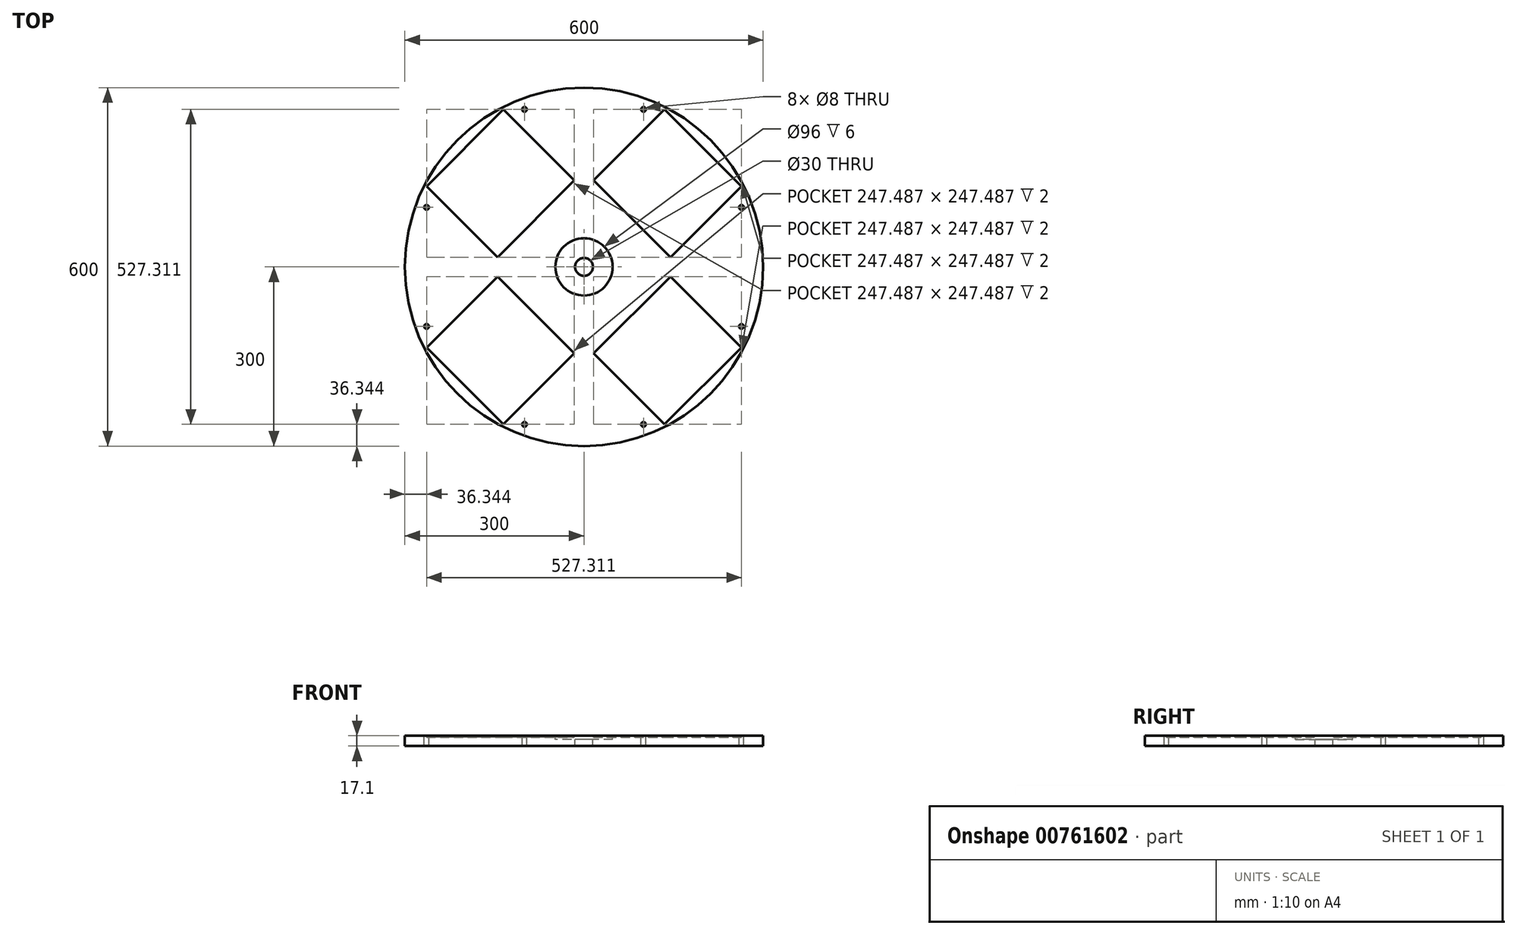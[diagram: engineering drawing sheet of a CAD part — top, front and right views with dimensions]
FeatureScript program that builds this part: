
annotation { "Feature Type Name" : "Feature", "Feature Type Description" : "" }
export const myFeature = defineFeature(function(context is Context, id is Id, definition is map)
    precondition{}
    {
        {
            var Q0;
            Q0=qCreatedBy(makeId("Top.planeOp"),FACE);
            var sketch = newSketch(context, id + "F0", { "sketchPlane" : qUnion([Q0])});
            skCircle(sketch, "E0", {"center": v(0, 0) * mm, "radius": 300 * mm});
            skSolve(sketch);
        }
        {
            var Q0;
            Q0 = qSketchRegion(id + "F0", true);
            var Q1;
            Q1=makeQuery(id+"F0.imprint","IMPRINT",FACE,{"disambiguationData":[TD([[makeQuery(id+"F0.imprint","IMPRINT",EDGE,{"derivedFrom":sQuery(id+"F0.wireOp",EDGE,"AllwrVL7-AkE9-LfNM-VB61-ajPjN6t2vvd7.bottom")}),-1.0]])]});
            var Q2;
            Q2=makeQuery(id+"F0.imprint","IMPRINT",FACE,{"disambiguationData":[TD([[makeQuery(id+"F0.imprint","IMPRINT",EDGE,{"derivedFrom":sQuery(id+"F0.wireOp",EDGE,"5d97284d-aa32-4368-b48b-b87623f71f09.3.0")}),1.0]])]});
            var Q3;
            Q3=makeQuery(id+"F0.imprint","IMPRINT",FACE,{"disambiguationData":[TD([[makeQuery(id+"F0.imprint","IMPRINT",EDGE,{"derivedFrom":sQuery(id+"F0.wireOp",EDGE,"5d97284d-aa32-4368-b48b-b87623f71f09.2.0")}),1.0]])]});
            var Q4;
            Q4=makeQuery(id+"F0.imprint","IMPRINT",FACE,{"disambiguationData":[TD([[makeQuery(id+"F0.imprint","IMPRINT",EDGE,{"derivedFrom":sQuery(id+"F0.wireOp",EDGE,"5d97284d-aa32-4368-b48b-b87623f71f09.1.0")}),1.0]])]});
            extrude(context, id + "F1", {"entities" : qUnion([Q0, Q1, Q2, Q3, Q4]), "depth" : 17.1 * mm, "offsetDistance" : 25 * mm});
        }
        {
            var Q0;
            Q0=makeQuery(id+"F1.opExtrude","CAP_FACE",FACE,{"disambiguationData":[OSD([sQuery(id+"F0.wireOp",EDGE,"E0"),sQuery(id+"F0.wireOp",EDGE,"m1Yok3GX-FKcm-f6FL-vg4J-QwZKevZHBzbs.bottom"),sQuery(id+"F0.wireOp",EDGE,"m1Yok3GX-FKcm-f6FL-vg4J-QwZKevZHBzbs.top"),sQuery(id+"F0.wireOp",EDGE,"m1Yok3GX-FKcm-f6FL-vg4J-QwZKevZHBzbs.left"),sQuery(id+"F0.wireOp",EDGE,"m1Yok3GX-FKcm-f6FL-vg4J-QwZKevZHBzbs.right"),sQuery(id+"F0.wireOp",EDGE,"c3f3dfe4-16c6-495d-901e-fd32c168dcf2.1.0"),sQuery(id+"F0.wireOp",EDGE,"c3f3dfe4-16c6-495d-901e-fd32c168dcf2.1.1"),sQuery(id+"F0.wireOp",EDGE,"c3f3dfe4-16c6-495d-901e-fd32c168dcf2.1.2"),sQuery(id+"F0.wireOp",EDGE,"c3f3dfe4-16c6-495d-901e-fd32c168dcf2.1.3"),sQuery(id+"F0.wireOp",EDGE,"c3f3dfe4-16c6-495d-901e-fd32c168dcf2.2.0"),sQuery(id+"F0.wireOp",EDGE,"c3f3dfe4-16c6-495d-901e-fd32c168dcf2.2.1"),sQuery(id+"F0.wireOp",EDGE,"c3f3dfe4-16c6-495d-901e-fd32c168dcf2.2.2"),sQuery(id+"F0.wireOp",EDGE,"c3f3dfe4-16c6-495d-901e-fd32c168dcf2.2.3"),sQuery(id+"F0.wireOp",EDGE,"c3f3dfe4-16c6-495d-901e-fd32c168dcf2.3.0"),sQuery(id+"F0.wireOp",EDGE,"c3f3dfe4-16c6-495d-901e-fd32c168dcf2.3.1"),sQuery(id+"F0.wireOp",EDGE,"c3f3dfe4-16c6-495d-901e-fd32c168dcf2.3.2"),sQuery(id+"F0.wireOp",EDGE,"c3f3dfe4-16c6-495d-901e-fd32c168dcf2.3.3"),sQuery(id+"F0.wireOp",EDGE,"GgWlmIyM-ttYd-3ydM-N6fe-A3lpZPIy1D6L"),sQuery(id+"F0.wireOp",EDGE,"be6c052b-b5ba-4b0f-ad13-1682f92d27ab0.MirrorC"),sQuery(id+"F0.wireOp",EDGE,"65b34546-e90f-493b-8633-af6543c614b7.1.0"),sQuery(id+"F0.wireOp",EDGE,"65b34546-e90f-493b-8633-af6543c614b7.1.1"),sQuery(id+"F0.wireOp",EDGE,"65b34546-e90f-493b-8633-af6543c614b7.2.0"),sQuery(id+"F0.wireOp",EDGE,"65b34546-e90f-493b-8633-af6543c614b7.2.1"),sQuery(id+"F0.wireOp",EDGE,"65b34546-e90f-493b-8633-af6543c614b7.3.0"),sQuery(id+"F0.wireOp",EDGE,"65b34546-e90f-493b-8633-af6543c614b7.3.1"),sQuery(id+"F0.wireOp",EDGE,"Zrx7hTxE-zzg4-Czgn-36LA-upzHOa7QcTNY"),sQuery(id+"F0.wireOp",EDGE,"a1d9c7c6-3c1d-4fec-942b-8c6368d16cfa0.MirrorC"),sQuery(id+"F0.wireOp",EDGE,"64f4d127-5a3c-484e-af48-e4f96c13fd4a.1.0"),sQuery(id+"F0.wireOp",EDGE,"64f4d127-5a3c-484e-af48-e4f96c13fd4a.1.1"),sQuery(id+"F0.wireOp",EDGE,"64f4d127-5a3c-484e-af48-e4f96c13fd4a.2.0"),sQuery(id+"F0.wireOp",EDGE,"64f4d127-5a3c-484e-af48-e4f96c13fd4a.2.1"),sQuery(id+"F0.wireOp",EDGE,"64f4d127-5a3c-484e-af48-e4f96c13fd4a.3.0"),sQuery(id+"F0.wireOp",EDGE,"64f4d127-5a3c-484e-af48-e4f96c13fd4a.3.1")])],"isStart":false});
            var sketch = newSketch(context, id + "F2", { "sketchPlane" : qUnion([Q0])});
            skLineSegment(sketch, "E1", {"start": v(0, 0) * mm, "end": v(-212.13, -212.13) * mm, "construction": true});
            skLineSegment(sketch, "E2", {"start": v(0, 0) * mm, "end": v(-300, 0) * mm, "construction": true});
            skLineSegment(sketch, "E3", {"start": v(-263.66, -134.96) * mm, "end": v(-134.96, -263.66) * mm});
            skLineSegment(sketch, "E4", {"start": v(-134.96, -263.66) * mm, "end": v(-16.17, -144.86) * mm});
            skLineSegment(sketch, "E5", {"start": v(-16.17, -144.86) * mm, "end": v(-144.86, -16.17) * mm});
            skLineSegment(sketch, "E6", {"start": v(-144.86, -16.17) * mm, "end": v(-263.66, -134.96) * mm});
            skPoint(sketch, "E7", {"position": v(-199.3, -199.3) * mm});
            skLineSegment(sketch, "E8", {"start": v(0, 0) * mm, "end": v(212.13, 212.13) * mm, "construction": true});
            skLineSegment(sketch, "E9", {"start": v(0, 0) * mm, "end": v(212.13, -212.13) * mm, "construction": true});
            skLineSegment(sketch, "E10", {"start": v(-263.66, -134.96) * mm, "end": v(-266.48, -137.8) * mm});
            skLineSegment(sketch, "E11.1.0", {"start": v(16.17, -144.86) * mm, "end": v(134.96, -263.66) * mm});
            skLineSegment(sketch, "E11.1.1", {"start": v(144.86, -16.17) * mm, "end": v(16.17, -144.86) * mm});
            skLineSegment(sketch, "E11.1.2", {"start": v(263.66, -134.96) * mm, "end": v(144.86, -16.17) * mm});
            skLineSegment(sketch, "E11.1.3", {"start": v(134.96, -263.66) * mm, "end": v(263.66, -134.96) * mm});
            skLineSegment(sketch, "E11.2.0", {"start": v(144.86, 16.17) * mm, "end": v(263.66, 134.96) * mm});
            skLineSegment(sketch, "E11.2.1", {"start": v(16.17, 144.86) * mm, "end": v(144.86, 16.17) * mm});
            skLineSegment(sketch, "E11.2.2", {"start": v(134.96, 263.66) * mm, "end": v(16.17, 144.86) * mm});
            skLineSegment(sketch, "E11.2.3", {"start": v(263.66, 134.96) * mm, "end": v(134.96, 263.66) * mm});
            skLineSegment(sketch, "E11.3.0", {"start": v(-16.17, 144.86) * mm, "end": v(-134.96, 263.66) * mm});
            skLineSegment(sketch, "E11.3.1", {"start": v(-144.86, 16.17) * mm, "end": v(-16.17, 144.86) * mm});
            skLineSegment(sketch, "E11.3.2", {"start": v(-263.66, 134.96) * mm, "end": v(-144.86, 16.17) * mm});
            skLineSegment(sketch, "E11.3.3", {"start": v(-134.96, 263.66) * mm, "end": v(-263.66, 134.96) * mm});
            skPoint(sketch, "E11.center", {"position": v(0, 0) * mm});
            skSolve(sketch);
        }
        {
            var Q0;
            Q0=qSketchRegion(id+"F2",true);
            extrude(context, id + "F3", {"entities" : qUnion([Q0]), "operationType" : NewBodyOperationType.REMOVE, "oppositeDirection" : true, "depth" : 2 * mm, "offsetDistance" : 25 * mm});
        }
        {
            var Q0;
            Q0=makeQuery(id+"F1.opExtrude","CAP_FACE",FACE,{"disambiguationData":[OSD([sQuery(id+"F0.wireOp",EDGE,"E0"),sQuery(id+"F0.wireOp",EDGE,"m1Yok3GX-FKcm-f6FL-vg4J-QwZKevZHBzbs.bottom"),sQuery(id+"F0.wireOp",EDGE,"m1Yok3GX-FKcm-f6FL-vg4J-QwZKevZHBzbs.top"),sQuery(id+"F0.wireOp",EDGE,"m1Yok3GX-FKcm-f6FL-vg4J-QwZKevZHBzbs.left"),sQuery(id+"F0.wireOp",EDGE,"m1Yok3GX-FKcm-f6FL-vg4J-QwZKevZHBzbs.right"),sQuery(id+"F0.wireOp",EDGE,"c3f3dfe4-16c6-495d-901e-fd32c168dcf2.1.0"),sQuery(id+"F0.wireOp",EDGE,"c3f3dfe4-16c6-495d-901e-fd32c168dcf2.1.1"),sQuery(id+"F0.wireOp",EDGE,"c3f3dfe4-16c6-495d-901e-fd32c168dcf2.1.2"),sQuery(id+"F0.wireOp",EDGE,"c3f3dfe4-16c6-495d-901e-fd32c168dcf2.1.3"),sQuery(id+"F0.wireOp",EDGE,"c3f3dfe4-16c6-495d-901e-fd32c168dcf2.2.0"),sQuery(id+"F0.wireOp",EDGE,"c3f3dfe4-16c6-495d-901e-fd32c168dcf2.2.1"),sQuery(id+"F0.wireOp",EDGE,"c3f3dfe4-16c6-495d-901e-fd32c168dcf2.2.2"),sQuery(id+"F0.wireOp",EDGE,"c3f3dfe4-16c6-495d-901e-fd32c168dcf2.2.3"),sQuery(id+"F0.wireOp",EDGE,"c3f3dfe4-16c6-495d-901e-fd32c168dcf2.3.0"),sQuery(id+"F0.wireOp",EDGE,"c3f3dfe4-16c6-495d-901e-fd32c168dcf2.3.1"),sQuery(id+"F0.wireOp",EDGE,"c3f3dfe4-16c6-495d-901e-fd32c168dcf2.3.2"),sQuery(id+"F0.wireOp",EDGE,"c3f3dfe4-16c6-495d-901e-fd32c168dcf2.3.3"),sQuery(id+"F0.wireOp",EDGE,"GgWlmIyM-ttYd-3ydM-N6fe-A3lpZPIy1D6L"),sQuery(id+"F0.wireOp",EDGE,"be6c052b-b5ba-4b0f-ad13-1682f92d27ab0.MirrorC"),sQuery(id+"F0.wireOp",EDGE,"65b34546-e90f-493b-8633-af6543c614b7.1.0"),sQuery(id+"F0.wireOp",EDGE,"65b34546-e90f-493b-8633-af6543c614b7.1.1"),sQuery(id+"F0.wireOp",EDGE,"65b34546-e90f-493b-8633-af6543c614b7.2.0"),sQuery(id+"F0.wireOp",EDGE,"65b34546-e90f-493b-8633-af6543c614b7.2.1"),sQuery(id+"F0.wireOp",EDGE,"65b34546-e90f-493b-8633-af6543c614b7.3.0"),sQuery(id+"F0.wireOp",EDGE,"65b34546-e90f-493b-8633-af6543c614b7.3.1"),sQuery(id+"F0.wireOp",EDGE,"Zrx7hTxE-zzg4-Czgn-36LA-upzHOa7QcTNY"),sQuery(id+"F0.wireOp",EDGE,"a1d9c7c6-3c1d-4fec-942b-8c6368d16cfa0.MirrorC"),sQuery(id+"F0.wireOp",EDGE,"64f4d127-5a3c-484e-af48-e4f96c13fd4a.1.0"),sQuery(id+"F0.wireOp",EDGE,"64f4d127-5a3c-484e-af48-e4f96c13fd4a.1.1"),sQuery(id+"F0.wireOp",EDGE,"64f4d127-5a3c-484e-af48-e4f96c13fd4a.2.0"),sQuery(id+"F0.wireOp",EDGE,"64f4d127-5a3c-484e-af48-e4f96c13fd4a.2.1"),sQuery(id+"F0.wireOp",EDGE,"64f4d127-5a3c-484e-af48-e4f96c13fd4a.3.0"),sQuery(id+"F0.wireOp",EDGE,"64f4d127-5a3c-484e-af48-e4f96c13fd4a.3.1"),sQuery(id+"F0.wireOp",EDGE,"AllwrVL7-AkE9-LfNM-VB61-ajPjN6t2vvd7.bottom"),sQuery(id+"F0.wireOp",EDGE,"AllwrVL7-AkE9-LfNM-VB61-ajPjN6t2vvd7.top"),sQuery(id+"F0.wireOp",EDGE,"AllwrVL7-AkE9-LfNM-VB61-ajPjN6t2vvd7.left"),sQuery(id+"F0.wireOp",EDGE,"AllwrVL7-AkE9-LfNM-VB61-ajPjN6t2vvd7.right"),sQuery(id+"F0.wireOp",EDGE,"vhIM6kYj-bil8-T5aC-Hw9W-HzG7wACOchpu.bottom"),sQuery(id+"F0.wireOp",EDGE,"vhIM6kYj-bil8-T5aC-Hw9W-HzG7wACOchpu.top"),sQuery(id+"F0.wireOp",EDGE,"vhIM6kYj-bil8-T5aC-Hw9W-HzG7wACOchpu.left"),sQuery(id+"F0.wireOp",EDGE,"vhIM6kYj-bil8-T5aC-Hw9W-HzG7wACOchpu.right"),sQuery(id+"F0.wireOp",EDGE,"e5db2dc1-b70e-487e-85e1-c1db5f647828.1.0"),sQuery(id+"F0.wireOp",EDGE,"e5db2dc1-b70e-487e-85e1-c1db5f647828.1.1"),sQuery(id+"F0.wireOp",EDGE,"e5db2dc1-b70e-487e-85e1-c1db5f647828.1.2"),sQuery(id+"F0.wireOp",EDGE,"e5db2dc1-b70e-487e-85e1-c1db5f647828.1.3"),sQuery(id+"F0.wireOp",EDGE,"e5db2dc1-b70e-487e-85e1-c1db5f647828.1.4"),sQuery(id+"F0.wireOp",EDGE,"e5db2dc1-b70e-487e-85e1-c1db5f647828.1.5"),sQuery(id+"F0.wireOp",EDGE,"e5db2dc1-b70e-487e-85e1-c1db5f647828.1.6"),sQuery(id+"F0.wireOp",EDGE,"e5db2dc1-b70e-487e-85e1-c1db5f647828.1.7"),sQuery(id+"F0.wireOp",EDGE,"e5db2dc1-b70e-487e-85e1-c1db5f647828.2.0"),sQuery(id+"F0.wireOp",EDGE,"e5db2dc1-b70e-487e-85e1-c1db5f647828.2.1"),sQuery(id+"F0.wireOp",EDGE,"e5db2dc1-b70e-487e-85e1-c1db5f647828.2.2"),sQuery(id+"F0.wireOp",EDGE,"e5db2dc1-b70e-487e-85e1-c1db5f647828.2.3"),sQuery(id+"F0.wireOp",EDGE,"e5db2dc1-b70e-487e-85e1-c1db5f647828.2.4"),sQuery(id+"F0.wireOp",EDGE,"e5db2dc1-b70e-487e-85e1-c1db5f647828.2.5"),sQuery(id+"F0.wireOp",EDGE,"e5db2dc1-b70e-487e-85e1-c1db5f647828.2.6"),sQuery(id+"F0.wireOp",EDGE,"e5db2dc1-b70e-487e-85e1-c1db5f647828.2.7"),sQuery(id+"F0.wireOp",EDGE,"e5db2dc1-b70e-487e-85e1-c1db5f647828.3.0"),sQuery(id+"F0.wireOp",EDGE,"e5db2dc1-b70e-487e-85e1-c1db5f647828.3.1"),sQuery(id+"F0.wireOp",EDGE,"e5db2dc1-b70e-487e-85e1-c1db5f647828.3.2"),sQuery(id+"F0.wireOp",EDGE,"e5db2dc1-b70e-487e-85e1-c1db5f647828.3.3"),sQuery(id+"F0.wireOp",EDGE,"e5db2dc1-b70e-487e-85e1-c1db5f647828.3.4"),sQuery(id+"F0.wireOp",EDGE,"e5db2dc1-b70e-487e-85e1-c1db5f647828.3.5"),sQuery(id+"F0.wireOp",EDGE,"e5db2dc1-b70e-487e-85e1-c1db5f647828.3.6"),sQuery(id+"F0.wireOp",EDGE,"e5db2dc1-b70e-487e-85e1-c1db5f647828.3.7")])],"isStart":false});
            var sketch = newSketch(context, id + "F4", { "sketchPlane" : qUnion([Q0])});
            skLineSegment(sketch, "E12", {"start": v(-263.66, -99.6) * mm, "end": v(-245.98, -117.28) * mm, "construction": true});
            skCircle(sketch, "E13", {"center": v(-263.66, -99.6) * mm, "radius": 4 * mm});
            skLineSegment(sketch, "E14", {"start": v(-99.6, -263.66) * mm, "end": v(-117.28, -245.98) * mm, "construction": true});
            skCircle(sketch, "E15", {"center": v(-99.6, -263.66) * mm, "radius": 4 * mm});
            skCircle(sketch, "E16.1.0", {"center": v(99.6, -263.66) * mm, "radius": 4 * mm});
            skCircle(sketch, "E16.1.1", {"center": v(263.66, -99.6) * mm, "radius": 4 * mm});
            skCircle(sketch, "E16.2.0", {"center": v(263.66, 99.6) * mm, "radius": 4 * mm});
            skCircle(sketch, "E16.2.1", {"center": v(99.6, 263.66) * mm, "radius": 4 * mm});
            skCircle(sketch, "E16.3.0", {"center": v(-99.6, 263.66) * mm, "radius": 4 * mm});
            skCircle(sketch, "E16.3.1", {"center": v(-263.66, 99.6) * mm, "radius": 4 * mm});
            skPoint(sketch, "E16.center", {"position": v(0, 0) * mm});
            skSolve(sketch);
        }
        {
            var Q0;
            Q0=qSketchRegion(id+"F4",true);
            extrude(context, id + "F5", {"entities" : qUnion([Q0]), "operationType" : NewBodyOperationType.REMOVE, "oppositeDirection" : true, "depth" : 25 * mm, "offsetDistance" : 25 * mm});
        }
        {
            var Q0;
            Q0=makeQuery(id+"F1.opExtrude","CAP_FACE",FACE,{"disambiguationData":[OSD([sQuery(id+"F0.wireOp",EDGE,"E0")])],"isStart":false});
            var sketch = newSketch(context, id + "F6", { "sketchPlane" : qUnion([Q0])});
            skCircle(sketch, "E17", {"center": v(0, 0) * mm, "radius": 48 * mm});
            skSolve(sketch);
        }
        {
            var Q0;
            Q0=makeQuery(id+"F6.imprint","IMPRINT",FACE,{"disambiguationData":[TD([[makeQuery(id+"F6.imprint","IMPRINT",EDGE,{"derivedFrom":sQuery(id+"F6.wireOp",EDGE,"E17")}),1.0]])]});
            extrude(context, id + "F7", {"entities" : qUnion([Q0]), "operationType" : NewBodyOperationType.REMOVE, "oppositeDirection" : true, "depth" : 6 * mm, "offsetDistance" : 25 * mm});
        }
        {
            var Q0;
            Q0=makeQuery(id+"F7.boolean.opBoolean","COPY",FACE,{"derivedFrom":makeQuery(id+"F7.opExtrude","CAP_FACE",FACE,{"disambiguationData":[OSD([sQuery(id+"F6.wireOp",EDGE,"E17")])],"isStart":false})});
            var sketch = newSketch(context, id + "F8", { "sketchPlane" : qUnion([Q0])});
            skCircle(sketch, "E18", {"center": v(0, 0) * mm, "radius": 15 * mm});
            skSolve(sketch);
        }
        {
            var Q0;
            Q0=makeQuery(id+"F8.imprint","IMPRINT",FACE,{"disambiguationData":[TD([[makeQuery(id+"F8.imprint","IMPRINT",EDGE,{"derivedFrom":sQuery(id+"F8.wireOp",EDGE,"E18")}),1.0]])]});
            extrude(context, id + "F9", {"entities" : qUnion([Q0]), "operationType" : NewBodyOperationType.REMOVE, "endBound" : BoundingType.THROUGH_ALL, "oppositeDirection" : true, "depth" : 25 * mm, "offsetDistance" : 25 * mm});
        }
    });
